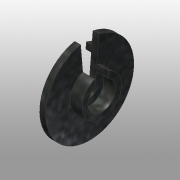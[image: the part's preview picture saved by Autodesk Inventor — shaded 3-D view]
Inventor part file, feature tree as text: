
AUTODESK INVENTOR PART (.ipt)
format: ipt  version: 2016 (Build 200138000, 138)  size: 146,944 bytes
history: native  units: mm
features: sketch x2, revolve x1, extrude x1
ambient origin geometry x8: Origin, YZ Plane, XZ Plane, XY Plane, X Axis, Y Axis, Z Axis, Center Point
bodies: Body1 (feature_tree)
feature tree (4):
  revolve  "Revolution2"  [1 undecoded]
  extrude  "Extrusion1"  Depth=1.65mm
  sketch  "Sketch1"  dims[d0=5.1mm d1=4.25mm]
  sketch  "Sketch2"  dims[d2=3.0mm d3=1.65mm d4=1.3mm d5=2.5mm d6=0.0mm d7=9.55mm d8=7.0mm d9=5.7mm d11=90.0deg d12=0.872665mm d13=0.872665mm d14=2.5mm d15=1.25mm d16=10.0mm d17=0.0mm]
note: 1 required parameter value undecoded (feature->parameter linkage not recoverable at this tier; creation-order binding heuristic only, values carry confidence <= 0.55)
